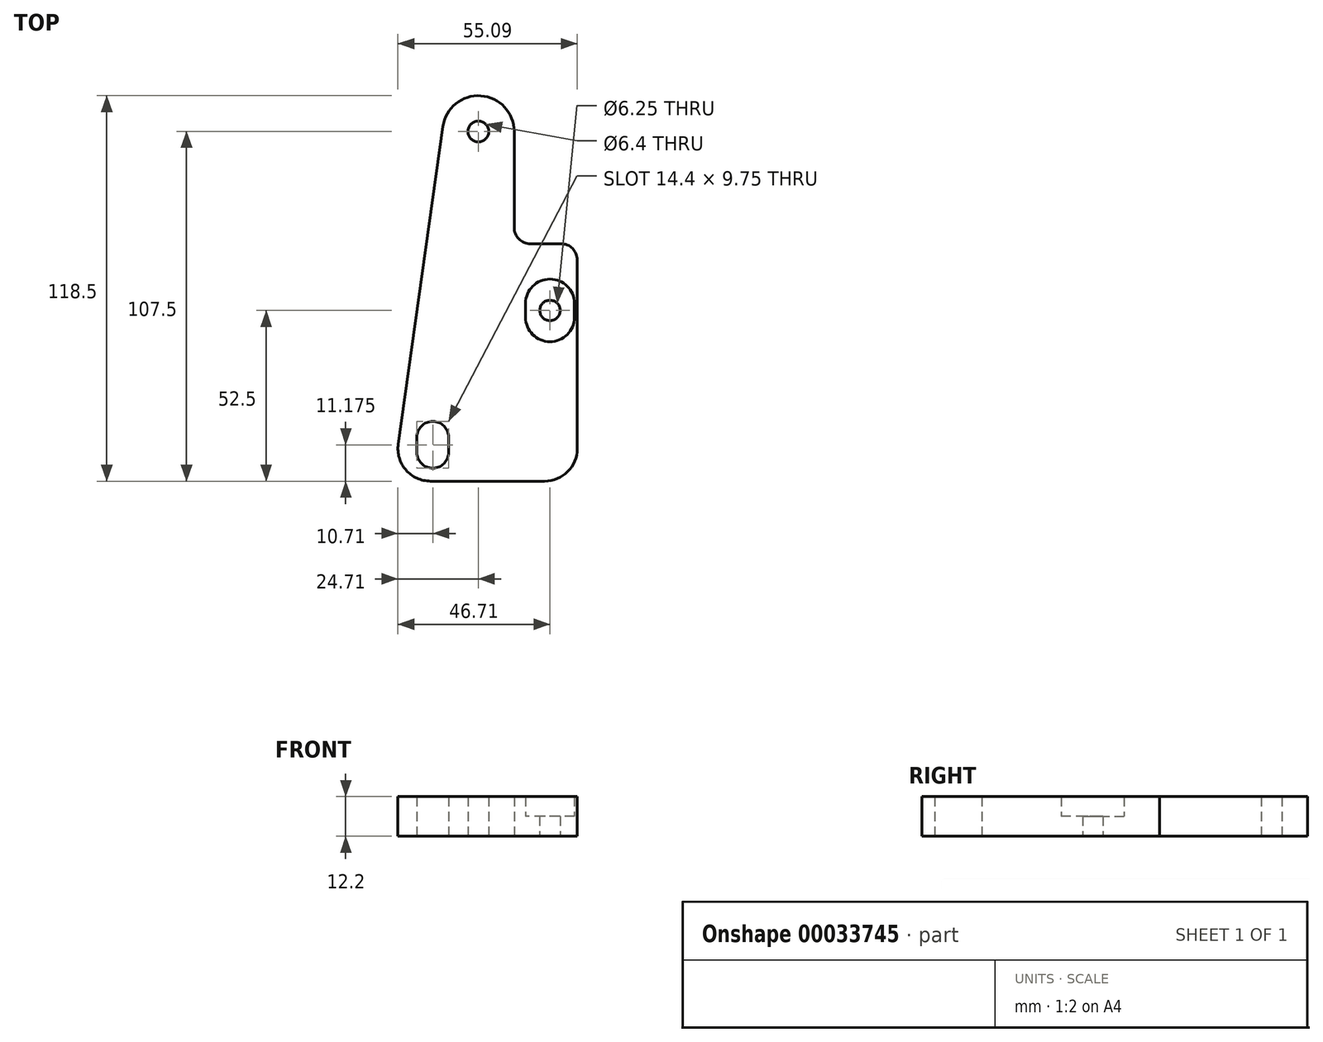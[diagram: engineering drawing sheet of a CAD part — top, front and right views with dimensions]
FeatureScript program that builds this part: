
annotation { "Feature Type Name" : "Feature", "Feature Type Description" : "" }
export const myFeature = defineFeature(function(context is Context, id is Id, definition is map)
    precondition{}
    {
        {
            var Q0;
            Q0=qCreatedBy(makeId("Top.planeOp"),FACE);
            var sketch = newSketch(context, id + "F0", { "sketchPlane" : qUnion([Q0])});
            skCircle(sketch, "E0", {"center": v(0, 0) * mm, "radius": 3.2 * mm});
            skArc(sketch, "E1", {"start": v(11, 0) * mm, "mid": v(0.77, 10.97) * mm, "end": v(-10.9, 1.53) * mm});
            skLineSegment(sketch, "E2", {"start": v(-14, -94) * mm, "end": v(-14, -98.65) * mm, "construction": true});
            skArc(sketch, "E3.0.startCap", {"start": v(-18.87, -94) * mm, "mid": v(-14, -89.12) * mm, "end": v(-9.12, -94) * mm});
            skArc(sketch, "E3.0.endCap", {"start": v(-9.12, -98.65) * mm, "mid": v(-14, -103.53) * mm, "end": v(-18.87, -98.65) * mm});
            skLineSegment(sketch, "E3.0.left", {"start": v(-9.12, -94) * mm, "end": v(-9.12, -98.65) * mm});
            skLineSegment(sketch, "E3.0.right", {"start": v(-18.87, -94) * mm, "end": v(-18.87, -98.65) * mm});
            skLineSegment(sketch, "E4", {"start": v(-14.71, -107.5) * mm, "end": v(20.38, -107.5) * mm});
            skLineSegment(sketch, "E5", {"start": v(-10.9, 1.53) * mm, "end": v(-24.62, -96.1) * mm});
            skLineSegment(sketch, "E6", {"start": v(11, 0) * mm, "end": v(11, -29.5) * mm});
            skArc(sketch, "E7.filletArc", {"start": v(-24.62, -96.1) * mm, "mid": v(-22.26, -104.06) * mm, "end": v(-14.71, -107.5) * mm});
            skLineSegment(sketch, "E8", {"start": v(16, -34.5) * mm, "end": v(25.38, -34.5) * mm});
            skLineSegment(sketch, "E9", {"start": v(30.38, -39.5) * mm, "end": v(30.38, -97.5) * mm});
            skPoint(sketch, "E10.visualSharp", {"position": v(11, -34.5) * mm});
            skArc(sketch, "E10.filletArc", {"start": v(11, -29.5) * mm, "mid": v(12.46, -33.04) * mm, "end": v(16, -34.5) * mm});
            skPoint(sketch, "E11.visualSharp", {"position": v(30.38, -34.5) * mm});
            skArc(sketch, "E11.filletArc", {"start": v(30.38, -39.5) * mm, "mid": v(28.92, -35.96) * mm, "end": v(25.38, -34.5) * mm});
            skPoint(sketch, "E12.newPointA", {"position": v(30.38, -114.38) * mm});
            skPoint(sketch, "E12.newPointB", {"position": v(30.38, -107.5) * mm});
            skArc(sketch, "E12.filletArc", {"start": v(20.38, -107.5) * mm, "mid": v(27.46, -104.57) * mm, "end": v(30.38, -97.5) * mm});
            skLineSegment(sketch, "E13", {"start": v(0, 0) * mm, "end": v(0, -77.2) * mm, "construction": true});
            skCircle(sketch, "E14", {"center": v(22, -55) * mm, "radius": 3.12 * mm});
            skSolve(sketch);
        }
        {
            var Q0;
            Q0 = qSketchRegion(id + "F0", true);
            extrude(context, id + "F1", {"entities" : qUnion([Q0]), "depth" : 6.2 * mm});
        }
        {
            var Q0;
            Q0=makeQuery(id+"F1.opExtrude","CAP_FACE",FACE,{"disambiguationData":[OSD([sQuery(id+"F0.wireOp",EDGE,"E0"),sQuery(id+"F0.wireOp",EDGE,"E1"),sQuery(id+"F0.wireOp",EDGE,"E3.0.startCap"),sQuery(id+"F0.wireOp",EDGE,"E3.0.endCap"),sQuery(id+"F0.wireOp",EDGE,"E3.0.left"),sQuery(id+"F0.wireOp",EDGE,"E3.0.right"),sQuery(id+"F0.wireOp",EDGE,"E4"),sQuery(id+"F0.wireOp",EDGE,"E5"),sQuery(id+"F0.wireOp",EDGE,"E6"),sQuery(id+"F0.wireOp",EDGE,"E7.filletArc"),sQuery(id+"F0.wireOp",EDGE,"E8"),sQuery(id+"F0.wireOp",EDGE,"E9"),sQuery(id+"F0.wireOp",EDGE,"E10.filletArc"),sQuery(id+"F0.wireOp",EDGE,"E11.filletArc"),sQuery(id+"F0.wireOp",EDGE,"E12.filletArc"),sQuery(id+"F0.wireOp",EDGE,"E14")])],"isStart":false});
            var sketch = newSketch(context, id + "F2", { "sketchPlane" : qUnion([Q0])});
            skLineSegment(sketch, "E15", {"start": v(22, -52.87) * mm, "end": v(22, -57.12) * mm, "construction": true});
            skPoint(sketch, "E16", {"position": v(22, -55) * mm});
            skArc(sketch, "E17.0.startCap", {"start": v(14.5, -52.87) * mm, "mid": v(22, -45.37) * mm, "end": v(29.5, -52.87) * mm});
            skArc(sketch, "E17.0.endCap", {"start": v(29.5, -57.13) * mm, "mid": v(22, -64.62) * mm, "end": v(14.5, -57.13) * mm});
            skLineSegment(sketch, "E17.0.left", {"start": v(29.5, -52.87) * mm, "end": v(29.5, -57.13) * mm});
            skLineSegment(sketch, "E17.0.right", {"start": v(14.5, -52.87) * mm, "end": v(14.5, -57.13) * mm});
            skSolve(sketch);
        }
        {
            var Q0;
            Q0=makeQuery(id+"F2.imprint","IMPRINT",FACE,{"disambiguationData":[TD([[makeQuery(id+"F2.imprint","IMPRINT",EDGE,{"derivedFrom":sQuery(id+"F2.wireOp",EDGE,"E17.0.startCap")}),-1.0]])]});
            extrude(context, id + "F3", {"entities" : qUnion([Q0]), "operationType" : NewBodyOperationType.ADD, "depth" : 6 * mm});
        }
    });
